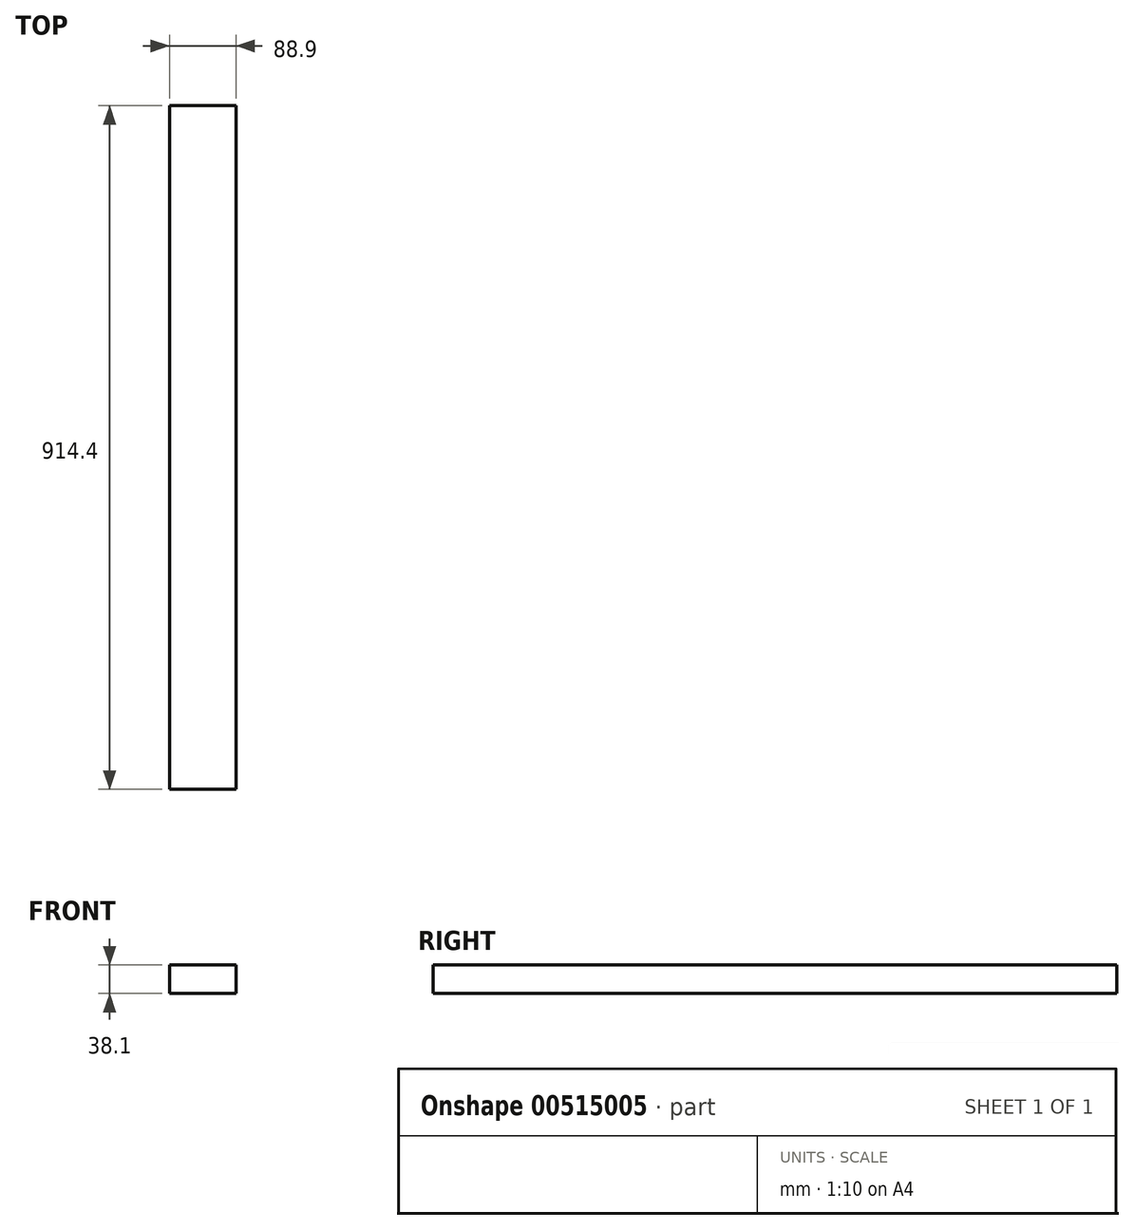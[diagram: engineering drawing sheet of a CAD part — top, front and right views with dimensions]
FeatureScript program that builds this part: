
annotation { "Feature Type Name" : "Feature", "Feature Type Description" : "" }
export const myFeature = defineFeature(function(context is Context, id is Id, definition is map)
    precondition{}
    {
        {
            var Q0;
            Q0=qCreatedBy(makeId("Top.planeOp"),FACE);
            var sketch = newSketch(context, id + "F0", { "sketchPlane" : qUnion([Q0])});
            skLineSegment(sketch, "E0.bottom", {"start": v(0, 1.64) * mm, "end": v(88.9, 1.64) * mm});
            skLineSegment(sketch, "E0.top", {"start": v(0, 916.04) * mm, "end": v(88.9, 916.04) * mm});
            skLineSegment(sketch, "E0.left", {"start": v(0, 1.64) * mm, "end": v(0, 916.04) * mm});
            skLineSegment(sketch, "E0.right", {"start": v(88.9, 1.64) * mm, "end": v(88.9, 916.04) * mm});
            skSolve(sketch);
        }
        {
            var Q0;
            Q0 = qSketchRegion(id + "F0", true);
            extrude(context, id + "F1", {"entities" : qUnion([Q0]), "depth" : 38.1 * mm, "offsetDistance" : 25.4 * mm});
        }
    });
